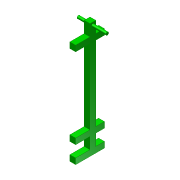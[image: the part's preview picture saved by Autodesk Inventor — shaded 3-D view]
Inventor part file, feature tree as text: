
AUTODESK INVENTOR PART (.ipt)
format: ipt  version: 2012 (Build 160160000, 160)  size: 113,152 bytes
history: native  units: in
note: dims shown in document units (in); Inventor stores cm internally (conversion verified against a paired STEP export)
features: extrude x3, sketch x3
ambient origin geometry x8: Origin, YZ Plane, XZ Plane, XY Plane, X Axis, Y Axis, Z Axis, Center Point
bodies: Solid1 (feature_tree)
feature tree (6):
  extrude  "Extrusion1"  Depth=1.0in
  extrude  "Extrusion2"  Depth=0.5in
  extrude  "Extrusion3"  Depth=0.5in
  sketch  "Sketch2"  dims[d0=1.0in d1=1.0in]
  sketch  "Sketch3"  dims[d2=20.0in d3=0.0in d4=0.5in]
  sketch  "Sketch4"  dims[d5=0.5in d6=0.5in d7=5.0in d8=0.0in d9=1.0in d10=2.0in d11=1.0in d13=13.0in d14=15.0in d15=5.0in d16=0.0in d17=1.0in d18=4.0in]
